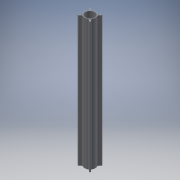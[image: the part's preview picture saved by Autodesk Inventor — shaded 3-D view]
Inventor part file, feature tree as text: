
AUTODESK INVENTOR PART (.ipt)
format: ipt  version: 2016 (Build 200138000, 138)  size: 145,920 bytes
history: native  units: mm
features: extrude x1, sketch x1
ambient origin geometry x8: Origin, YZ Plane, XZ Plane, XY Plane, X Axis, Y Axis, Z Axis, Center Point
bodies: Solid1 (feature_tree)
feature tree (2):
  extrude  "Extrusion1"  [1 undecoded]
  sketch  "Sketch1"  dims[d0=1000.0mm d1=0.0mm]
note: 1 required parameter value undecoded (feature->parameter linkage not recoverable at this tier; creation-order binding heuristic only, values carry confidence <= 0.55)
